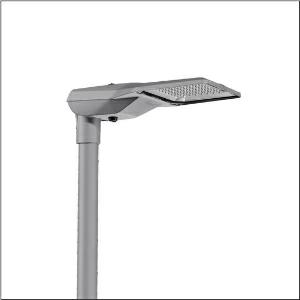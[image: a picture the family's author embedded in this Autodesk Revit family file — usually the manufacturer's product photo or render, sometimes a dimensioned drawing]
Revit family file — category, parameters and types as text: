
# Revit family: streetlight_sl_21_midi___st0_8a_5xe3c43t08mb_e12c
name_source: partatom
category: Lighting Fixtures
units: mm (PartAtom-declared; Revit-internal decimal feet)

## family parameters
Cut with Voids When Loaded = No
Host = Face
Light Source = No
Part Type = Normal
Room Calculation Point = No
Round Connector Dimension = Use Diameter
Shared = No

## types (1)
- --- (1 x LED, 20180 lm, 147 W, 4000K)
    Apparent Load = 147 VA
    CIE Flux Codes = 38 75 97 100 100
    Color Rendering = 70
    Color Temperature = 4000K
    Default Elevation = 1800 mm
    Description = Streetlight SL 21 midi, mast luminaire, primary light control with lens, of PMMA, primary optical cover: cover, of toughened safety glass, transparent, light distribution: ST0.8a, light emission: direct distribution, primary light characteristic: asymmetric, installation type: side-entry, post-top, LED, High Power LED, rated luminous flux: 20.180lm, luminous efficacy: 137lm/W, light colour: 740, colour temperature: 4000K, control: overheat protection, constant luminous flux control, time-dependent luminous flux control, flexible luminous flux parameterisation, presetting dimming logarithmic, mains connection: 230..240V, AC, 50/60Hz, start of lifetime: 147W, end of service life: 155W, reduction: 65W, luminaire housing, of diecast aluminium, powder-coated, Siteco® metallic grey (DB 702S), corrosivity category C5 mid according to DIN EN ISO 12944, please order mast flange separately, inclination adjustable: 0°, 5°, 10°, 15°, sealing non-destructively replaceable, multi-level sealing system, length: 644mm, width: 335mm, height: 110mm, mast flange for spigot size: 42mm (side-entry): 5XC10008XM4, 60/48mm (side-entry/post-top): 5XC10108XM2, 76/60mm (side-entry/post-top): 5XC10108XM1, Smart Interface below and above, protection rating (complete): IP66, insulation class (complete): insulation class II (safety insulation), certification: CE, ENEC, ENEC+, VDE, impact resistance: IK09, permissible operating ambient temperature for outdoor applications: -40..+50°C, standard-compliant lighting for roads and squares, packaging unit: 1 piece

Light Distribution: ST0.8a
    Height = 111 mm
    Lamp = 1 x LED
    Lamp Light Flux = 20180 lm
    Lamp Power = 147 W
    Lamp count = 1
    Length = 644 mm
    Luminous efficacy = 137 lm/W
    Manufacturer = Siteco
    ModVariant = No
    Model = 5XE3C43T08MB
    Number of Poles = 1
    OnlyDefault = Yes
    Power Factor = 1
    Product Name = Streetlight SL 21 midi | ST0.8a
    Product group = mast luminaire | pylon top
    ProductGroupID = 6100
    Protection Class = Protection class II
    Protection Degree = IP 66
    RLX_Detail_Level = 1
    RLX_Emergency_Light_Flux = 0 lm
    RLX_Emergency_Type = 0
    RLX_Emergency_Type_DB = No
    RlxData = <blob elided: 91165 chars, md5=f9552950>
    Socket = socket
    Standby Power = 0 W
    System Light Flux = 20180 lm
    System Power = 147 W
    Type Comments = factory setting: luminous flux: 100 % | dim-lin: 254 | 750 mA
    Type Image = l_1004304.jpg
    URL = http://relux.com
    VarID = @adj_137593
    Voltage = 0 V
    Weight = 0.00 kg
    Width = 336 mm

## geometry (parser evidence)
native form markers: Blend x4, Sweep x11
no freeform markers — native parametric forms only
